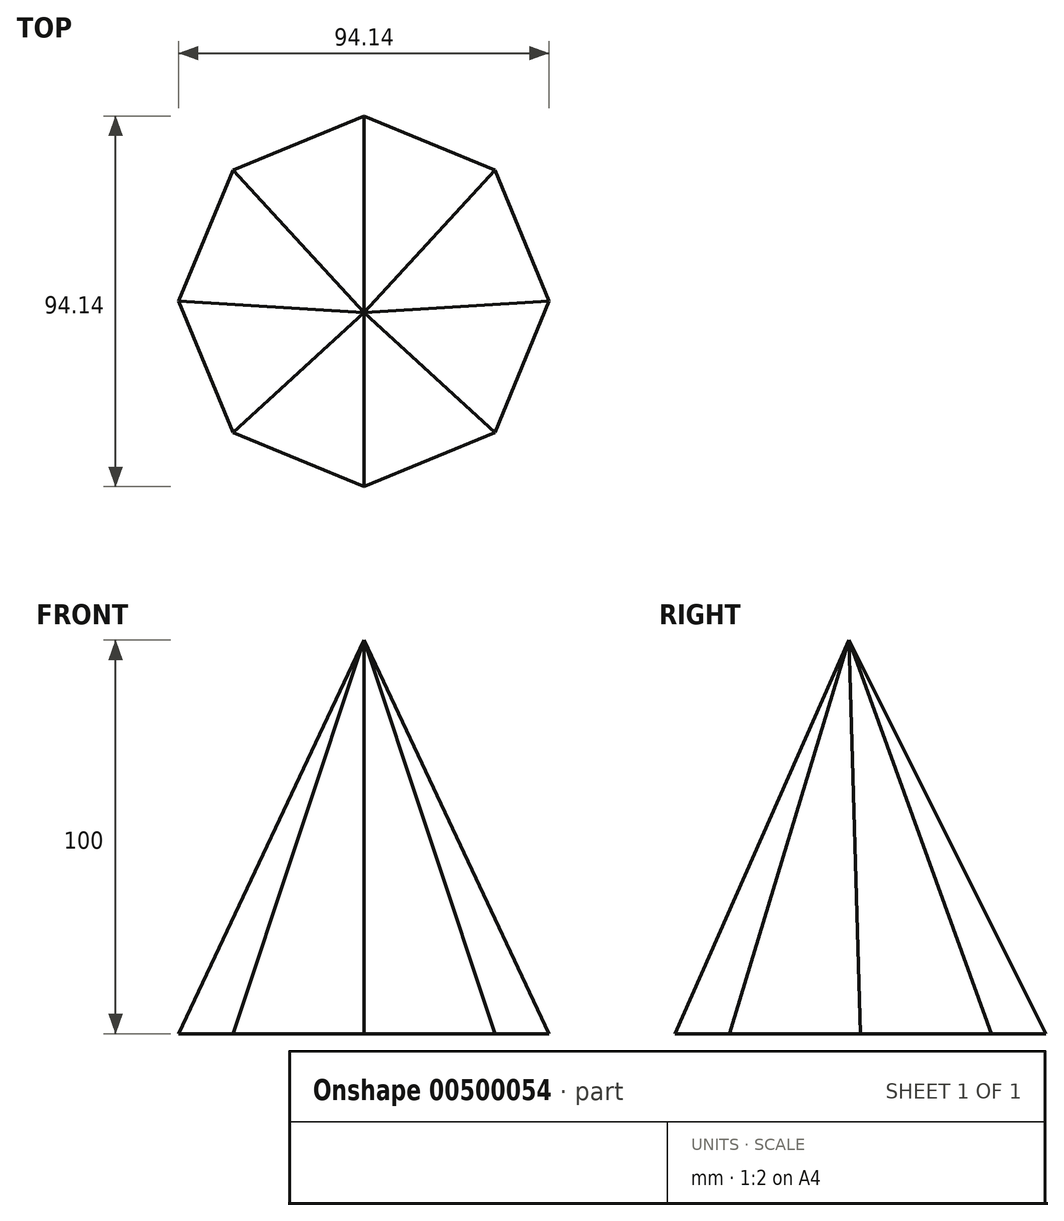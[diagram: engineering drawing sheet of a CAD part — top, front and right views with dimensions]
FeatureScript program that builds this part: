
annotation { "Feature Type Name" : "Feature", "Feature Type Description" : "" }
export const myFeature = defineFeature(function(context is Context, id is Id, definition is map)
    precondition{}
    {
        {
            var Q0;
            Q0=qCreatedBy(makeId("Top.planeOp"),FACE);
            var sketch = newSketch(context, id + "F0", { "sketchPlane" : qUnion([Q0])});
            skCircle(sketch, "E0.cCircle", {"center": v(0, 0) * mm, "radius": 47.07 * mm, "construction": true});
            skLineSegment(sketch, "E0.0", {"start": v(0, 47.07) * mm, "end": v(33.29, 33.29) * mm});
            skLineSegment(sketch, "E0.1", {"start": v(33.29, 33.29) * mm, "end": v(47.07, 0) * mm});
            skLineSegment(sketch, "E0.2", {"start": v(47.07, 0) * mm, "end": v(33.29, -33.29) * mm});
            skLineSegment(sketch, "E0.3", {"start": v(33.29, -33.29) * mm, "end": v(0, -47.07) * mm});
            skLineSegment(sketch, "E0.4", {"start": v(0, -47.07) * mm, "end": v(-33.29, -33.29) * mm});
            skLineSegment(sketch, "E0.5", {"start": v(-33.29, -33.29) * mm, "end": v(-47.07, 0) * mm});
            skLineSegment(sketch, "E0.6", {"start": v(-47.07, 0) * mm, "end": v(-33.29, 33.29) * mm});
            skLineSegment(sketch, "E0.7", {"start": v(-33.29, 33.29) * mm, "end": v(0, 47.07) * mm});
            skSolve(sketch);
        }
        {
            var Q0;
            Q0=qCreatedBy(makeId("Top.planeOp"),FACE);
            cPlane(context, id + "F1", {"entities" : qUnion([Q0]), "cplaneType" : CPlaneType.OFFSET, "offset" : 100 * mm, "width" : 152.4 * mm, "height" : 152.4 * mm});
        }
        {
            var Q0;
            Q0=qCreatedBy(id+"F1.planeOp",FACE);
            var sketch = newSketch(context, id + "F2", { "sketchPlane" : qUnion([Q0])});
            skPoint(sketch, "E1", {"position": v(0, -2.9) * mm});
            skSolve(sketch);
        }
        {
            var Q0;
            Q0=makeQuery(id+"F0.imprint","IMPRINT",FACE,{"disambiguationData":[TD([[makeQuery(id+"F0.imprint","IMPRINT",EDGE,{"derivedFrom":sQuery(id+"F0.wireOp",EDGE,"E0.0")}),-1.0]])]});
            var Q1;
            Q1=sQuery(id+"F2.wireOp",VERTEX,"E1");
            loft(context, id + "F3", {"sheetProfilesArray" : [{ "sheetProfileEntities" : qUnion([Q0]) }, { "sheetProfileEntities" : qUnion([Q1]) }]});
        }
    });
